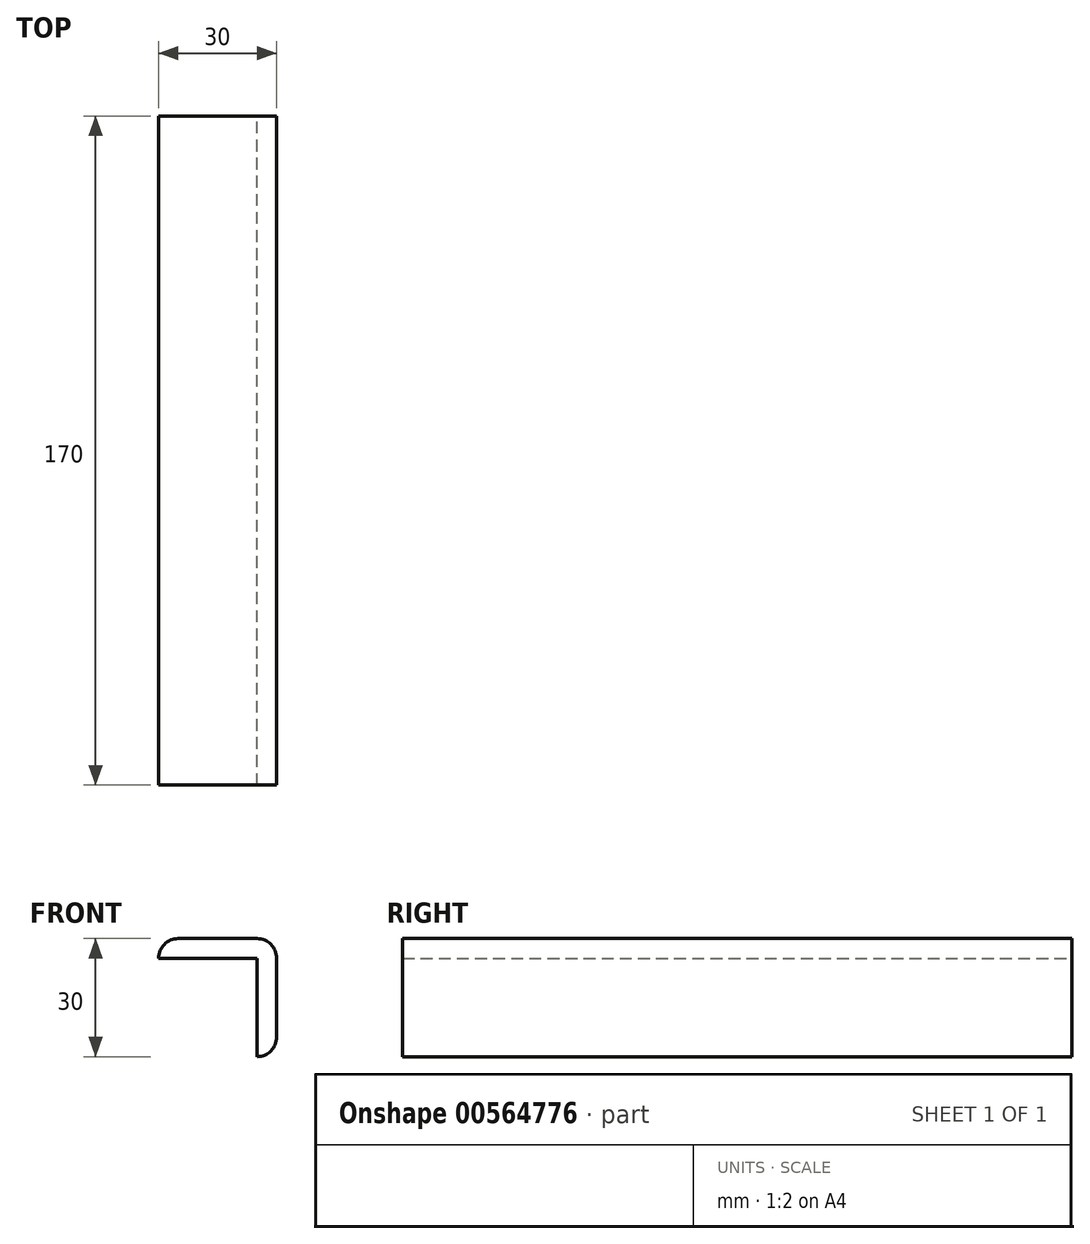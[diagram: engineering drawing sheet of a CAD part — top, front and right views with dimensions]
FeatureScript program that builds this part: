
annotation { "Feature Type Name" : "Feature", "Feature Type Description" : "" }
export const myFeature = defineFeature(function(context is Context, id is Id, definition is map)
    precondition{}
    {
        {
            var Q0;
            Q0=qCreatedBy(makeId("Front.planeOp"),FACE);
            var sketch = newSketch(context, id + "F0", { "sketchPlane" : qUnion([Q0])});
            skLineSegment(sketch, "E0.bottom", {"start": v(-15, 15) * mm, "end": v(15, 15) * mm});
            skLineSegment(sketch, "E0.top", {"start": v(10, -15) * mm, "end": v(15, -15) * mm});
            skLineSegment(sketch, "E0.left", {"start": v(-15, 15) * mm, "end": v(-15, 10) * mm});
            skLineSegment(sketch, "E0.right", {"start": v(15, 15) * mm, "end": v(15, -15) * mm});
            skPoint(sketch, "E0.middle", {"position": v(0, 0) * mm});
            skLineSegment(sketch, "E1.top", {"start": v(-15, 10) * mm, "end": v(10, 10) * mm});
            skLineSegment(sketch, "E1.right", {"start": v(10, -15) * mm, "end": v(10, 10) * mm});
            skPoint(sketch, "E2.orphan", {"position": v(-15, -15) * mm});
            skSolve(sketch);
        }
        {
            var Q0;
            Q0=makeQuery(id+"F0.imprint","IMPRINT",FACE,{"disambiguationData":[TD([[makeQuery(id+"F0.imprint","IMPRINT",EDGE,{"derivedFrom":sQuery(id+"F0.wireOp",EDGE,"E0.bottom")}),-1.0]])]});
            extrude(context, id + "F1", {"entities" : qUnion([Q0]), "endBound" : BoundingType.SYMMETRIC, "depth" : 170 * mm, "offsetDistance" : 25 * mm});
        }
        {
            var Q0;
            Q0=makeQuery(id+"F1.opExtrude","SWEPT_EDGE",EDGE,{"disambiguationData":[OSD([sQuery(id+"F0.wireOp",EDGE,"E0.bottom"),sQuery(id+"F0.wireOp",EDGE,"E0.left")])]});
            var Q1;
            Q1=makeQuery(id+"F1.opExtrude","SWEPT_EDGE",EDGE,{"disambiguationData":[OSD([sQuery(id+"F0.wireOp",EDGE,"E0.bottom"),sQuery(id+"F0.wireOp",EDGE,"E0.right")])]});
            var Q2;
            Q2=makeQuery(id+"F1.opExtrude","SWEPT_EDGE",EDGE,{"disambiguationData":[OSD([sQuery(id+"F0.wireOp",EDGE,"E0.top"),sQuery(id+"F0.wireOp",EDGE,"E0.right")])]});
            fillet(context, id + "F2", {"entities" : qUnion([Q0, Q1, Q2]), "radius" : 5 * mm, "tangentPropagation" : true, "allowEdgeOverflow" : false});
        }
    });
